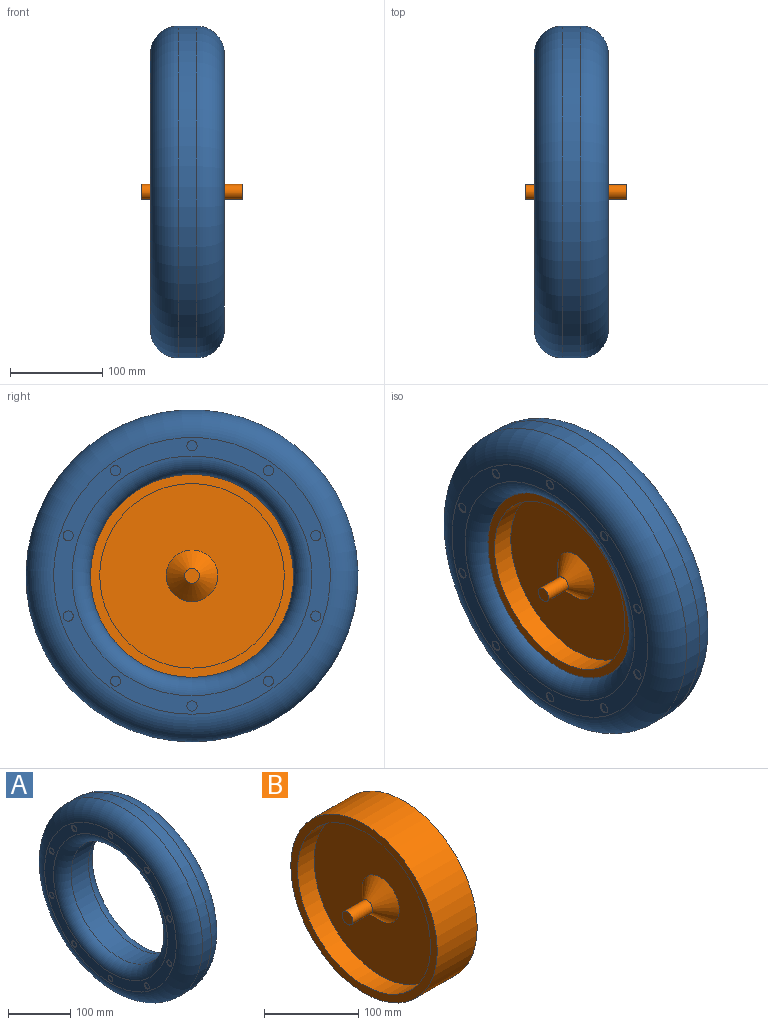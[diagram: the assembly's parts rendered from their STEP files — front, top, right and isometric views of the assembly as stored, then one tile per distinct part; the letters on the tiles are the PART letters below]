
ASSEMBLY  parts=2 mates=1
PART A: 48 faces, bbox 80x389.7x389.7 mm
  f0: cylinder r=5.53mm len=11.07mm, axis (-1,0,0), area 34.8mm2, adj f1,f39
  f1: plane 11.07x11.07mm, normal (-1,0,0), area 96.2mm2, adj f0
  f2: cylinder r=5.53mm len=11.07mm, axis (-1,0,0), area 34.8mm2, adj f3,f39
  f3: plane 11.07x11.07mm, normal (-1,0,0), area 96.2mm2, adj f2
  f4: cylinder r=5.53mm len=11.07mm, axis (-1,0,0), area 34.8mm2, adj f5,f39
  f5: plane 11.07x11.07mm, normal (-1,0,0), area 96.2mm2, adj f4
  f6: cylinder r=5.53mm len=11.07mm, axis (-1,0,0), area 34.8mm2, adj f7,f39
  f7: plane 11.07x11.07mm, normal (-1,0,0), area 96.2mm2, adj f6
  f8: cylinder r=5.53mm len=11.07mm, axis (-1,0,0), area 34.8mm2, adj f9,f39
  f9: plane 11.07x11.07mm, normal (-1,0,0), area 96.2mm2, adj f8
  f10: cylinder r=5.53mm len=11.07mm, axis (-1,0,0), area 34.8mm2, adj f11,f39
  f11: plane 11.07x11.07mm, normal (-1,0,0), area 96.2mm2, adj f10
  f12: cylinder r=5.53mm len=11.07mm, axis (-1,0,0), area 34.8mm2, adj f13,f39
  f13: plane 11.07x11.07mm, normal (-1,0,0), area 96.2mm2, adj f12
  f14: cylinder r=5.53mm len=11.07mm, axis (-1,0,0), area 34.8mm2, adj f15,f39
  f15: plane 11.07x11.07mm, normal (-1,0,0), area 96.2mm2, adj f14
  f16: cylinder r=5.53mm len=11.07mm, axis (-1,0,0), area 34.8mm2, adj f17,f39
  f17: plane 11.07x11.07mm, normal (-1,0,0), area 96.2mm2, adj f16
  f18: cylinder r=6.24mm len=12.48mm, axis (1,0,0), area 39.2mm2, adj f19,f38
  f19: plane 12.48x12.48mm, normal (1,0,0), area 122.3mm2, adj f18
  f20: cylinder r=6.24mm len=12.48mm, axis (1,0,0), area 39.2mm2, adj f21,f38
  f21: plane 12.48x12.48mm, normal (1,0,0), area 122.3mm2, adj f20
  f22: cylinder r=6.24mm len=12.48mm, axis (1,0,0), area 39.2mm2, adj f23,f38
  f23: plane 12.48x12.48mm, normal (1,0,0), area 122.3mm2, adj f22
  f24: cylinder r=6.24mm len=12.48mm, axis (1,0,0), area 39.2mm2, adj f25,f38
  f25: plane 12.48x12.48mm, normal (1,0,0), area 122.3mm2, adj f24
  f26: cylinder r=6.24mm len=12.48mm, axis (1,0,0), area 39.2mm2, adj f27,f38
  f27: plane 12.48x12.48mm, normal (1,0,0), area 122.3mm2, adj f26
  f28: cylinder r=6.24mm len=12.48mm, axis (1,0,0), area 39.2mm2, adj f29,f38
  f29: plane 12.48x12.48mm, normal (1,0,0), area 122.3mm2, adj f28
  f30: cylinder r=6.24mm len=12.48mm, axis (1,0,0), area 39.2mm2, adj f31,f38
  f31: plane 12.48x12.48mm, normal (1,0,0), area 122.3mm2, adj f30
  f32: cylinder r=6.24mm len=12.48mm, axis (1,0,0), area 39.2mm2, adj f33,f38
  f33: plane 12.48x12.48mm, normal (1,0,0), area 122.3mm2, adj f32
  f34: cylinder r=6.24mm len=12.48mm, axis (1,0,0), area 39.2mm2, adj f35,f38
  f35: plane 12.48x12.48mm, normal (1,0,0), area 122.3mm2, adj f34
  f36: cylinder r=110mm len=220mm, axis (-1,0,0), area 27646mm2, adj f42,f43
  f37: cylinder r=180mm len=360mm, axis (-1,0,0), area 22619.5mm2, adj f40,f41
  f38: plane 300x300mm, normal (1,0,0), area 16369.6mm2, adj f18,f20,f22,f24,f26,f28,f30,f32
  f39: plane 300x300mm, normal (-1,0,0), area 16630.9mm2, adj f0,f2,f4,f6,f8,f10,f12,f14
  f40: torus R=150mm, axis (1,0,0), area 50068.1mm2, adj f37,f39
  f41: torus R=150mm, axis (1,0,0), area 50068.1mm2, adj f37,f38
  f42: torus R=130mm, axis (1,0,0), area 23147.7mm2, adj f36,f39
  f43: torus R=130mm, axis (1,0,0), area 23147.7mm2, adj f36,f38
  f44: cylinder r=6.24mm len=12.48mm, axis (1,0,0), area 39.2mm2, adj f38,f45
  f45: plane 12.48x12.48mm, normal (1,0,0), area 122.3mm2, adj f44
  f46: cylinder r=5.53mm len=11.07mm, axis (-1,0,0), area 34.8mm2, adj f39,f47
  f47: plane 11.07x11.07mm, normal (-1,0,0), area 96.2mm2, adj f46
PART B: 13 faces, bbox 110x220x220 mm
  f0: cylinder r=8mm len=30mm, axis (-1,0,0), area 1508mm2, adj f1,f11
  f1: plane 16x16mm, normal (1,0,0), area 201.1mm2, adj f0
  f2: plane 200x200mm, normal (1,0,0), area 28952.9mm2, adj f4,f11
  f3: cylinder r=100mm len=200mm, axis (-1,0,0), area 15708mm2, adj f7,f10
  f4: cylinder r=100mm len=200mm, axis (-1,0,0), area 15708mm2, adj f2,f6
  f5: cylinder r=110mm len=220mm, axis (-1,0,0), area 41469mm2, adj f6,f7
  f6: plane 220x220mm, normal (1,0,0), area 6597.3mm2, adj f4,f5
  f7: plane 220x220mm, normal (-1,0,0), area 6597.3mm2, adj f3,f5
  f8: plane 16x16mm, normal (-1,0,0), area 201.1mm2, adj f9
  f9: cylinder r=8mm len=30mm, axis (-1,0,0), area 1508mm2, adj f8,f12
  f10: plane 200x200mm, normal (-1,0,0), area 28952.9mm2, adj f3,f12
  f11: cone r=8mm half-angle=45deg, axis (-1,0,0), area 3198.9mm2, adj f0,f2
  f12: cone r=28mm half-angle=45deg, axis (1,0,0), area 3198.9mm2, adj f9,f10
PLACE A t=(-192.23,-122.92,-29.27)mm
PLACE B t=(-187.23,-122.92,-29.27)mm
MATE fastened B.f0 <-> A.f36  axis (-1,0,0) through (-152.23,-122.92,-29.27)mm
